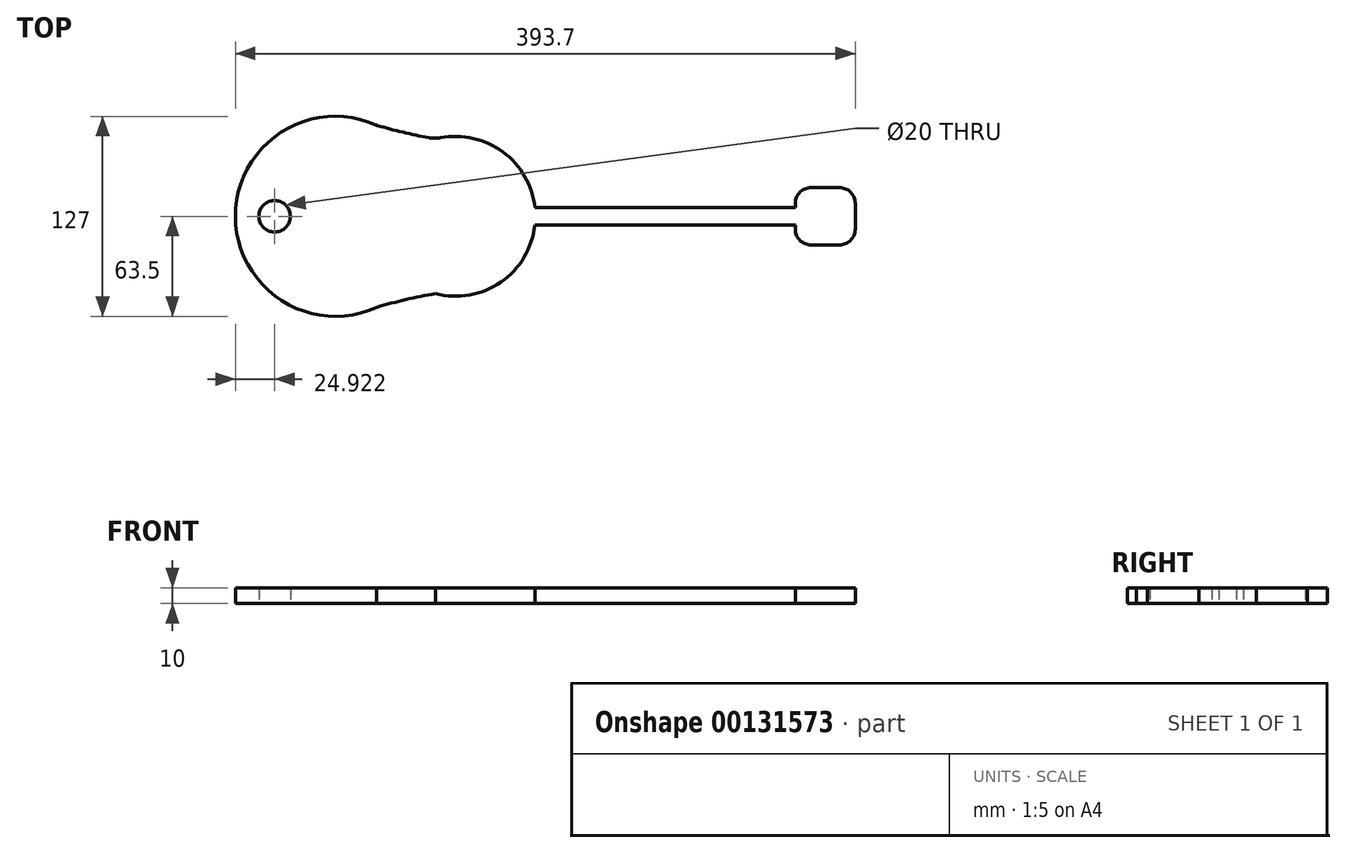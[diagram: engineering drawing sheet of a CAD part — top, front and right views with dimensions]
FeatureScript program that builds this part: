
annotation { "Feature Type Name" : "Feature", "Feature Type Description" : "" }
export const myFeature = defineFeature(function(context is Context, id is Id, definition is map)
    precondition{}
    {
        {
            var Q0;
            Q0=qCreatedBy(makeId("Top.planeOp"),FACE);
            var sketch = newSketch(context, id + "F0", { "sketchPlane" : qUnion([Q0])});
            skArc(sketch, "E0", {"start": v(13.56, 57.82) * mm, "mid": v(-76.2, 0) * mm, "end": v(13.56, -57.82) * mm});
            skLineSegment(sketch, "E1", {"start": v(-12.7, 0) * mm, "end": v(63.5, 0) * mm, "construction": true});
            skArc(sketch, "E2", {"start": v(0, 62.22) * mm, "mid": v(25.12, 54.6) * mm, "end": v(50.8, 49.19) * mm});
            skLineSegment(sketch, "E3", {"start": v(50.8, 49.19) * mm, "end": v(50.8, -89.08) * mm, "construction": true});
            skLineSegment(sketch, "E4", {"start": v(0, 62.22) * mm, "end": v(0, -130.63) * mm, "construction": true});
            skArc(sketch, "E5", {"start": v(50.8, -49.19) * mm, "mid": v(25.12, -54.6) * mm, "end": v(0, -62.22) * mm});
            skLineSegment(sketch, "E6", {"start": v(63.5, 0) * mm, "end": v(279.4, 0) * mm, "construction": true});
            skLineSegment(sketch, "E7", {"start": v(114, 5.51) * mm, "end": v(279.4, 5.51) * mm});
            skLineSegment(sketch, "E8", {"start": v(279.4, 5.51) * mm, "end": v(279.4, 0) * mm});
            skLineSegment(sketch, "E9.MirrorCS", {"start": v(114, -5.51) * mm, "end": v(279.4, -5.51) * mm});
            skLineSegment(sketch, "E10.MirrorCS", {"start": v(279.4, -5.51) * mm, "end": v(279.4, 0) * mm});
            skLineSegment(sketch, "E11", {"start": v(279.4, 5.51) * mm, "end": v(279.4, 18.21) * mm});
            skLineSegment(sketch, "E12", {"start": v(279.4, 18.21) * mm, "end": v(317.5, 18.21) * mm});
            skLineSegment(sketch, "E13", {"start": v(317.5, 18.21) * mm, "end": v(317.5, -18.21) * mm});
            skLineSegment(sketch, "E14", {"start": v(317.5, -18.21) * mm, "end": v(279.4, -18.21) * mm});
            skLineSegment(sketch, "E15", {"start": v(279.4, -18.21) * mm, "end": v(279.4, -5.51) * mm});
            skArc(sketch, "E16.trimOffspring", {"start": v(50.8, -49.19) * mm, "mid": v(114.3, 0) * mm, "end": v(50.8, 49.19) * mm});
            skCircle(sketch, "E17", {"center": v(-51.28, 0) * mm, "radius": 10 * mm});
            skSolve(sketch);
        }
        {
            var Q0;
            Q0 = qSketchRegion(id + "F0", true);
            extrude(context, id + "F1", {"entities" : qUnion([Q0]), "depth" : 10 * mm});
        }
        {
            var Q0;
            Q0=makeQuery(id+"F1.opExtrude","SWEPT_EDGE",EDGE,{"disambiguationData":[OSD([sQuery(id+"F0.wireOp",EDGE,"E0"),sQuery(id+"F0.wireOp",EDGE,"E2")])]});
            fillet(context, id + "F2", {"entities" : qUnion([Q0]), "radius" : 5 * mm, "tangentPropagation" : true, "allowEdgeOverflow" : false});
        }
        {
            var Q0;
            Q0=makeQuery(id+"F1.opExtrude","SWEPT_EDGE",EDGE,{"disambiguationData":[OSD([sQuery(id+"F0.wireOp",EDGE,"E2"),sQuery(id+"F0.wireOp",EDGE,"E16.trimOffspring")])]});
            fillet(context, id + "F3", {"entities" : qUnion([Q0]), "radius" : 20 * mm, "tangentPropagation" : true, "allowEdgeOverflow" : false});
        }
        {
            var Q0;
            Q0=makeQuery(id+"F1.opExtrude","SWEPT_EDGE",EDGE,{"disambiguationData":[OSD([sQuery(id+"F0.wireOp",EDGE,"E12"),sQuery(id+"F0.wireOp",EDGE,"E13")])]});
            var Q1;
            Q1=makeQuery(id+"F1.opExtrude","SWEPT_EDGE",EDGE,{"disambiguationData":[OSD([sQuery(id+"F0.wireOp",EDGE,"E11"),sQuery(id+"F0.wireOp",EDGE,"E12")])]});
            fillet(context, id + "F4", {"entities" : qUnion([Q0, Q1]), "radius" : 10 * mm, "tangentPropagation" : true, "allowEdgeOverflow" : false});
        }
        {
            var Q0;
            Q0=makeQuery(id+"F1.opExtrude","SWEPT_EDGE",EDGE,{"disambiguationData":[OSD([sQuery(id+"F0.wireOp",EDGE,"E13"),sQuery(id+"F0.wireOp",EDGE,"E14")])]});
            var Q1;
            Q1=makeQuery(id+"F1.opExtrude","SWEPT_EDGE",EDGE,{"disambiguationData":[OSD([sQuery(id+"F0.wireOp",EDGE,"E14"),sQuery(id+"F0.wireOp",EDGE,"E15")])]});
            fillet(context, id + "F5", {"entities" : qUnion([Q0, Q1]), "radius" : 10 * mm, "tangentPropagation" : true, "allowEdgeOverflow" : false});
        }
    });
